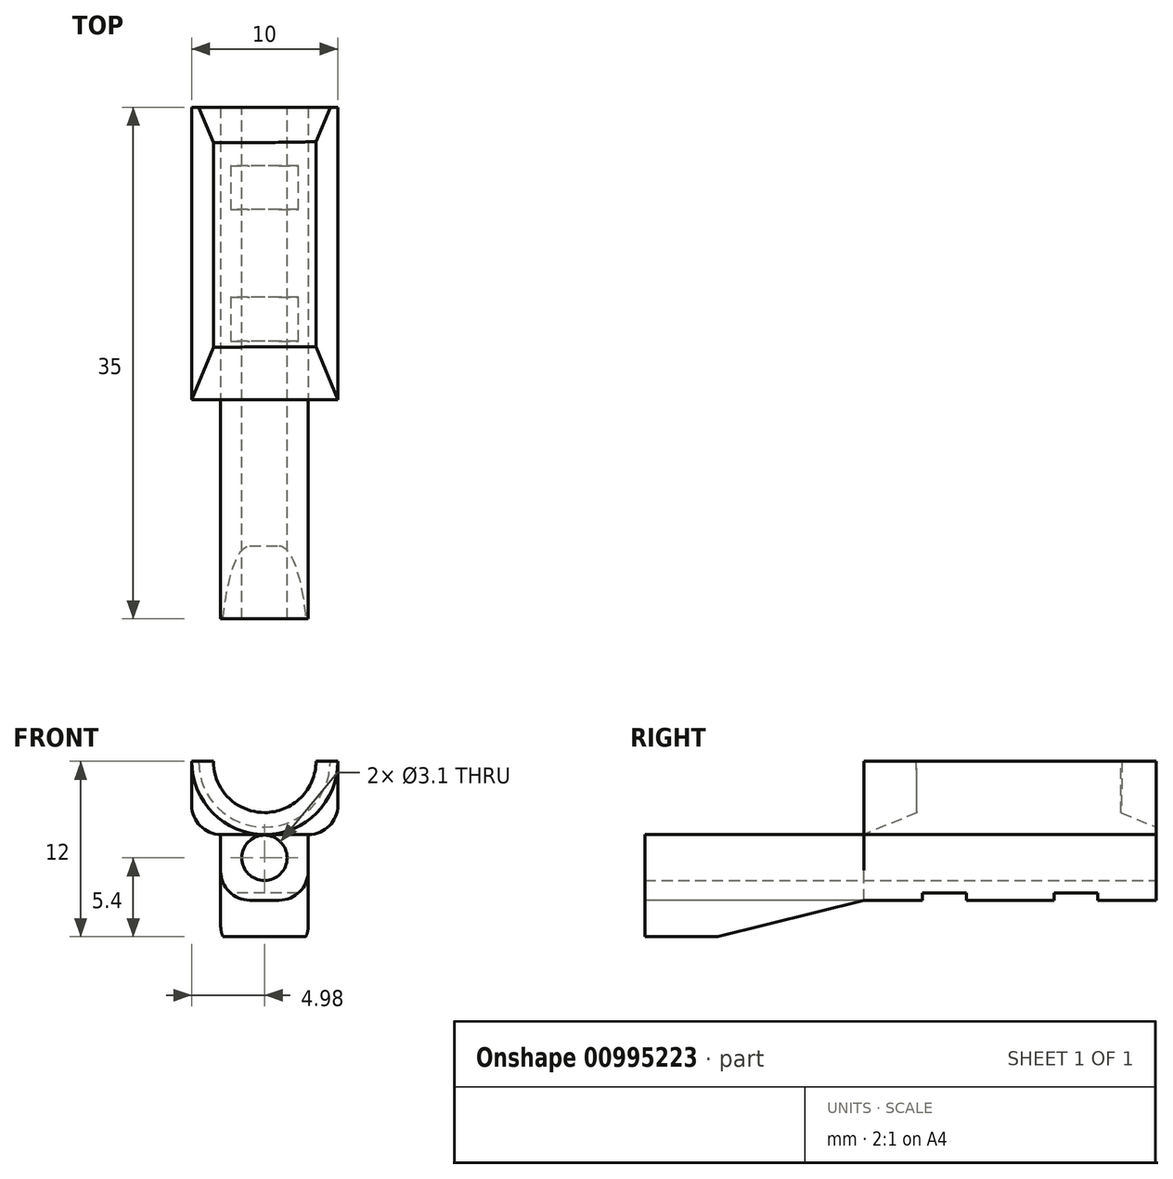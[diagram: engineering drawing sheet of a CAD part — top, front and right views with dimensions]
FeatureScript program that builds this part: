
annotation { "Feature Type Name" : "Feature", "Feature Type Description" : "" }
export const myFeature = defineFeature(function(context is Context, id is Id, definition is map)
    precondition{}
    {
        {
            var Q0;
            Q0=qCreatedBy(makeId("Top.planeOp"),FACE);
            var sketch = newSketch(context, id + "F0", { "sketchPlane" : qUnion([Q0])});
            skLineSegment(sketch, "E0.bottom", {"start": v(-4.98, 7.48) * mm, "end": v(5.02, 7.48) * mm});
            skLineSegment(sketch, "E0.top", {"start": v(-4.98, -12.52) * mm, "end": v(5.02, -12.52) * mm});
            skLineSegment(sketch, "E0.left", {"start": v(-4.98, 7.48) * mm, "end": v(-4.98, -12.52) * mm});
            skLineSegment(sketch, "E0.right", {"start": v(5.02, 7.48) * mm, "end": v(5.02, -12.52) * mm});
            skSolve(sketch);
        }
        {
            var Q0;
            Q0=makeQuery(id+"F0.imprint","IMPRINT",FACE,{"disambiguationData":[TD([[makeQuery(id+"F0.imprint","IMPRINT",EDGE,{"derivedFrom":sQuery(id+"F0.wireOp",EDGE,"E0.bottom")}),-1.0]])]});
            extrude(context, id + "F1", {"entities" : qUnion([Q0]), "depth" : 5 * mm, "offsetDistance" : 25 * mm});
        }
        {
            var Q0;
            Q0=makeQuery(id+"F1.opExtrude","SWEPT_FACE",FACE,{"disambiguationData":[OSD([sQuery(id+"F0.wireOp",EDGE,"E0.top")])]});
            var sketch = newSketch(context, id + "F2", { "sketchPlane" : qUnion([Q0])});
            skPoint(sketch, "E1", {"position": v(0.02, 5) * mm});
            skSolve(sketch);
        }
        {
            var Q0;
            Q0=makeQuery(id+"F1.opExtrude","SWEPT_FACE",FACE,{"disambiguationData":[OSD([sQuery(id+"F0.wireOp",EDGE,"E0.bottom")])]});
            var sketch = newSketch(context, id + "F3", { "sketchPlane" : qUnion([Q0])});
            skPoint(sketch, "E2", {"position": v(0, 5) * mm});
            skSolve(sketch);
        }
        {
            var Q0;
            Q0=sQuery(id+"F2.wireOp",VERTEX,"E1");
            var Q1;
            Q1=makeQuery(id+"F1.opExtrude","SWEPT_BODY",BODY,{"disambiguationData":[OSD([sQuery(id+"F0.wireOp",EDGE,"E0.bottom"),sQuery(id+"F0.wireOp",EDGE,"E0.top"),sQuery(id+"F0.wireOp",EDGE,"E0.left"),sQuery(id+"F0.wireOp",EDGE,"E0.right")])]});
            hole(context, id + "F4", {"style" : HoleStyle.C_SINK, "endStyle" : HoleEndStyle.THROUGH, "holeDiameter" : 7 * mm, "cSinkDiameter" : 10 * mm, "cSinkAngle" : 45 * degree, "majorDiameter" : 5 * mm, "isTappedThrough" : true, "tappedDepth" : 12 * mm, "tapClearance" : 3, "locations" : qUnion([Q0]), "scope" : qUnion([Q1])});
        }
        {
            var Q0;
            Q0=sQuery(id+"F3.wireOp",VERTEX,"E2");
            var Q1;
            Q1=makeQuery(id+"F1.opExtrude","SWEPT_BODY",BODY,{"disambiguationData":[OSD([sQuery(id+"F0.wireOp",EDGE,"E0.bottom"),sQuery(id+"F0.wireOp",EDGE,"E0.top"),sQuery(id+"F0.wireOp",EDGE,"E0.left"),sQuery(id+"F0.wireOp",EDGE,"E0.right")])]});
            hole(context, id + "F5", {"style" : HoleStyle.C_SINK, "endStyle" : HoleEndStyle.THROUGH, "holeDiameter" : 7 * mm, "cSinkDiameter" : 9 * mm, "cSinkAngle" : 45 * degree, "majorDiameter" : 5 * mm, "isTappedThrough" : true, "tappedDepth" : 12 * mm, "tapClearance" : 3, "locations" : qUnion([Q0]), "scope" : qUnion([Q1])});
        }
        {
            var Q0;
            Q0=makeQuery(id+"F1.opExtrude","CAP_FACE",FACE,{"disambiguationData":[OSD([sQuery(id+"F0.wireOp",EDGE,"E0.bottom"),sQuery(id+"F0.wireOp",EDGE,"E0.top"),sQuery(id+"F0.wireOp",EDGE,"E0.left"),sQuery(id+"F0.wireOp",EDGE,"E0.right")])],"isStart":true});
            var sketch = newSketch(context, id + "F6", { "sketchPlane" : qUnion([Q0])});
            skLineSegment(sketch, "E3.bottom", {"start": v(-3, -7.48) * mm, "end": v(3, -7.48) * mm});
            skLineSegment(sketch, "E3.top", {"start": v(-3, 12.52) * mm, "end": v(3, 12.52) * mm});
            skLineSegment(sketch, "E3.left", {"start": v(-3, -7.48) * mm, "end": v(-3, 12.52) * mm});
            skLineSegment(sketch, "E3.right", {"start": v(3, -7.48) * mm, "end": v(3, 12.52) * mm});
            skLineSegment(sketch, "E4.left", {"start": v(-3, 12.52) * mm, "end": v(-3, 12.52) * mm});
            skLineSegment(sketch, "E4.right", {"start": v(3, 12.52) * mm, "end": v(3, 12.52) * mm});
            skLineSegment(sketch, "E5.top", {"start": v(-3, 27.52) * mm, "end": v(3, 27.52) * mm});
            skLineSegment(sketch, "E5.left", {"start": v(-3, 12.52) * mm, "end": v(-3, 27.52) * mm});
            skLineSegment(sketch, "E5.right", {"start": v(3, 12.52) * mm, "end": v(3, 27.52) * mm});
            skSolve(sketch);
        }
        {
            var Q0;
            Q0=makeQuery(id+"F6.imprint","IMPRINT",FACE,{"disambiguationData":[TD([[makeQuery(id+"F6.imprint","IMPRINT",EDGE,{"derivedFrom":sQuery(id+"F6.wireOp",EDGE,"E5.top")}),-1.0]])]});
            extrude(context, id + "F7", {"entities" : qUnion([Q0]), "depth" : 7 * mm, "offsetDistance" : 25 * mm});
        }
        {
            var Q0;
            Q0 = qSketchRegion(id + "F6", true);
            extrude(context, id + "F8", {"entities" : qUnion([Q0]), "depth" : 4.5 * mm, "offsetDistance" : 25 * mm});
        }
        {
            var Q0;
            Q0=makeQuery(id+"F7.opExtrude","CAP_EDGE",EDGE,{"disambiguationData":[OSD([sQuery(id+"F6.wireOp",EDGE,"E3.top")])],"isStart":false});
            chamfer(context, id + "F9", {"entities" : qUnion([Q0]), "chamferType" : ChamferType.TWO_OFFSETS, "width1" : 10 * mm, "oppositeDirection" : false, "width2" : 2.5 * mm, "tangentPropagation" : true});
        }
        {
            var Q0;
            Q0=makeQuery(id+"F8.opExtrude","SWEPT_FACE",FACE,{"disambiguationData":[OSD([sQuery(id+"F6.wireOp",EDGE,"E3.bottom")])]});
            var sketch = newSketch(context, id + "F10", { "sketchPlane" : qUnion([Q0])});
            skPoint(sketch, "E6", {"position": v(0, -1.6) * mm});
            skPoint(sketch, "E6.positionSnap0", {"position": v(0, -4.5) * mm});
            skSolve(sketch);
        }
        {
            var Q0;
            Q0=sQuery(id+"F10.wireOp",VERTEX,"E6");
            var Q1;
            Q1=makeQuery(id+"F7.opExtrude","SWEPT_BODY",BODY,{"disambiguationData":[OSD([sQuery(id+"F6.wireOp",EDGE,"E3.top"),sQuery(id+"F6.wireOp",EDGE,"E5.top"),sQuery(id+"F6.wireOp",EDGE,"E5.left"),sQuery(id+"F6.wireOp",EDGE,"E5.right")])]});
            var Q2;
            Q2=makeQuery(id+"F8.opExtrude","SWEPT_BODY",BODY,{"disambiguationData":[OSD([sQuery(id+"F6.wireOp",EDGE,"E3.bottom"),sQuery(id+"F6.wireOp",EDGE,"E3.left"),sQuery(id+"F6.wireOp",EDGE,"E3.right"),sQuery(id+"F6.wireOp",EDGE,"E5.top"),sQuery(id+"F6.wireOp",EDGE,"E5.left"),sQuery(id+"F6.wireOp",EDGE,"E5.right")])]});
            hole(context, id + "F11", {"style" : HoleStyle.SIMPLE, "endStyle" : HoleEndStyle.THROUGH, "holeDiameter" : 3.1 * mm, "majorDiameter" : 5 * mm, "isTappedThrough" : true, "tappedDepth" : 12 * mm, "tapClearance" : 3, "locations" : qUnion([Q0]), "scope" : qUnion([Q1, Q2])});
        }
        {
            var Q0;
            Q0=makeQuery(id+"F1.opExtrude","CAP_EDGE",EDGE,{"disambiguationData":[OSD([sQuery(id+"F0.wireOp",EDGE,"E0.left")])],"isStart":true});
            var Q1;
            Q1=makeQuery(id+"F1.opExtrude","CAP_EDGE",EDGE,{"disambiguationData":[OSD([sQuery(id+"F0.wireOp",EDGE,"E0.right")])],"isStart":true});
            fillet(context, id + "F12", {"entities" : qUnion([Q0, Q1]), "radius" : 2 * mm, "tangentPropagation" : true, "allowEdgeOverflow" : false});
        }
        {
            var Q0;
            Q0=makeQuery(id+"F8.opExtrude","CAP_EDGE",EDGE,{"disambiguationData":[OSD([sQuery(id+"F6.wireOp",EDGE,"E3.left"),sQuery(id+"F6.wireOp",EDGE,"E5.left")])],"isStart":false});
            var Q1;
            Q1=makeQuery(id+"F8.opExtrude","CAP_EDGE",EDGE,{"disambiguationData":[OSD([sQuery(id+"F6.wireOp",EDGE,"E3.right"),sQuery(id+"F6.wireOp",EDGE,"E5.right")])],"isStart":false});
            fillet(context, id + "F13", {"entities" : qUnion([Q0, Q1]), "radius" : 2 * mm, "tangentPropagation" : true, "allowEdgeOverflow" : false});
        }
        {
            var Q0;
            Q0=makeQuery(id+"F9.opChamfer","BLEND_EDGE",EDGE,{"blendedFrom":[makeQuery(id+"F7.opExtrude","CAP_EDGE",EDGE,{"disambiguationData":[OSD([sQuery(id+"F6.wireOp",EDGE,"E3.top")])],"isStart":false}),makeQuery(id+"F7.opExtrude","SWEPT_FACE",FACE,{"disambiguationData":[OSD([sQuery(id+"F6.wireOp",EDGE,"E5.left")])]})],"blendedInto":[makeQuery(id+"F7.opExtrude","SWEPT_FACE",FACE,{"disambiguationData":[OSD([sQuery(id+"F6.wireOp",EDGE,"E5.left")])]})]});
            var Q1;
            Q1=makeQuery(id+"F9.opChamfer","BLEND_EDGE",EDGE,{"blendedFrom":[makeQuery(id+"F7.opExtrude","CAP_EDGE",EDGE,{"disambiguationData":[OSD([sQuery(id+"F6.wireOp",EDGE,"E3.top")])],"isStart":false}),makeQuery(id+"F7.opExtrude","SWEPT_FACE",FACE,{"disambiguationData":[OSD([sQuery(id+"F6.wireOp",EDGE,"E5.right")])]})],"blendedInto":[makeQuery(id+"F7.opExtrude","SWEPT_FACE",FACE,{"disambiguationData":[OSD([sQuery(id+"F6.wireOp",EDGE,"E5.right")])]})]});
            fillet(context, id + "F14", {"entities" : qUnion([Q0, Q1]), "radius" : 2 * mm, "tangentPropagation" : true, "allowEdgeOverflow" : false});
        }
        {
            var Q0;
            Q0=makeQuery(id+"F8.opExtrude","CAP_FACE",FACE,{"disambiguationData":[OSD([sQuery(id+"F6.wireOp",EDGE,"E3.bottom"),sQuery(id+"F6.wireOp",EDGE,"E3.left"),sQuery(id+"F6.wireOp",EDGE,"E3.right"),sQuery(id+"F6.wireOp",EDGE,"E5.top"),sQuery(id+"F6.wireOp",EDGE,"E5.left"),sQuery(id+"F6.wireOp",EDGE,"E5.right")])],"isStart":false});
            var sketch = newSketch(context, id + "F15", { "sketchPlane" : qUnion([Q0])});
            skLineSegment(sketch, "E7.bottom", {"start": v(4.84, -3.48) * mm, "end": v(-5.16, -3.48) * mm});
            skLineSegment(sketch, "E7.top", {"start": v(4.84, -0.48) * mm, "end": v(-5.16, -0.48) * mm});
            skLineSegment(sketch, "E7.left", {"start": v(4.84, -3.48) * mm, "end": v(4.84, -0.48) * mm});
            skLineSegment(sketch, "E7.right", {"start": v(-5.16, -3.48) * mm, "end": v(-5.16, -0.48) * mm});
            skLineSegment(sketch, "E8.bottom", {"start": v(5.08, 5.52) * mm, "end": v(-4.92, 5.52) * mm});
            skLineSegment(sketch, "E8.top", {"start": v(5.08, 8.52) * mm, "end": v(-4.92, 8.52) * mm});
            skLineSegment(sketch, "E8.left", {"start": v(5.08, 5.52) * mm, "end": v(5.08, 8.52) * mm});
            skLineSegment(sketch, "E8.right", {"start": v(-4.92, 5.52) * mm, "end": v(-4.92, 8.52) * mm});
            skSolve(sketch);
        }
        {
            var Q0;
            Q0 = qSketchRegion(id + "F15", true);
            extrude(context, id + "F16", {"entities" : qUnion([Q0]), "operationType" : NewBodyOperationType.REMOVE, "oppositeDirection" : true, "depth" : 0.5 * mm, "offsetDistance" : 25 * mm});
        }
    });
